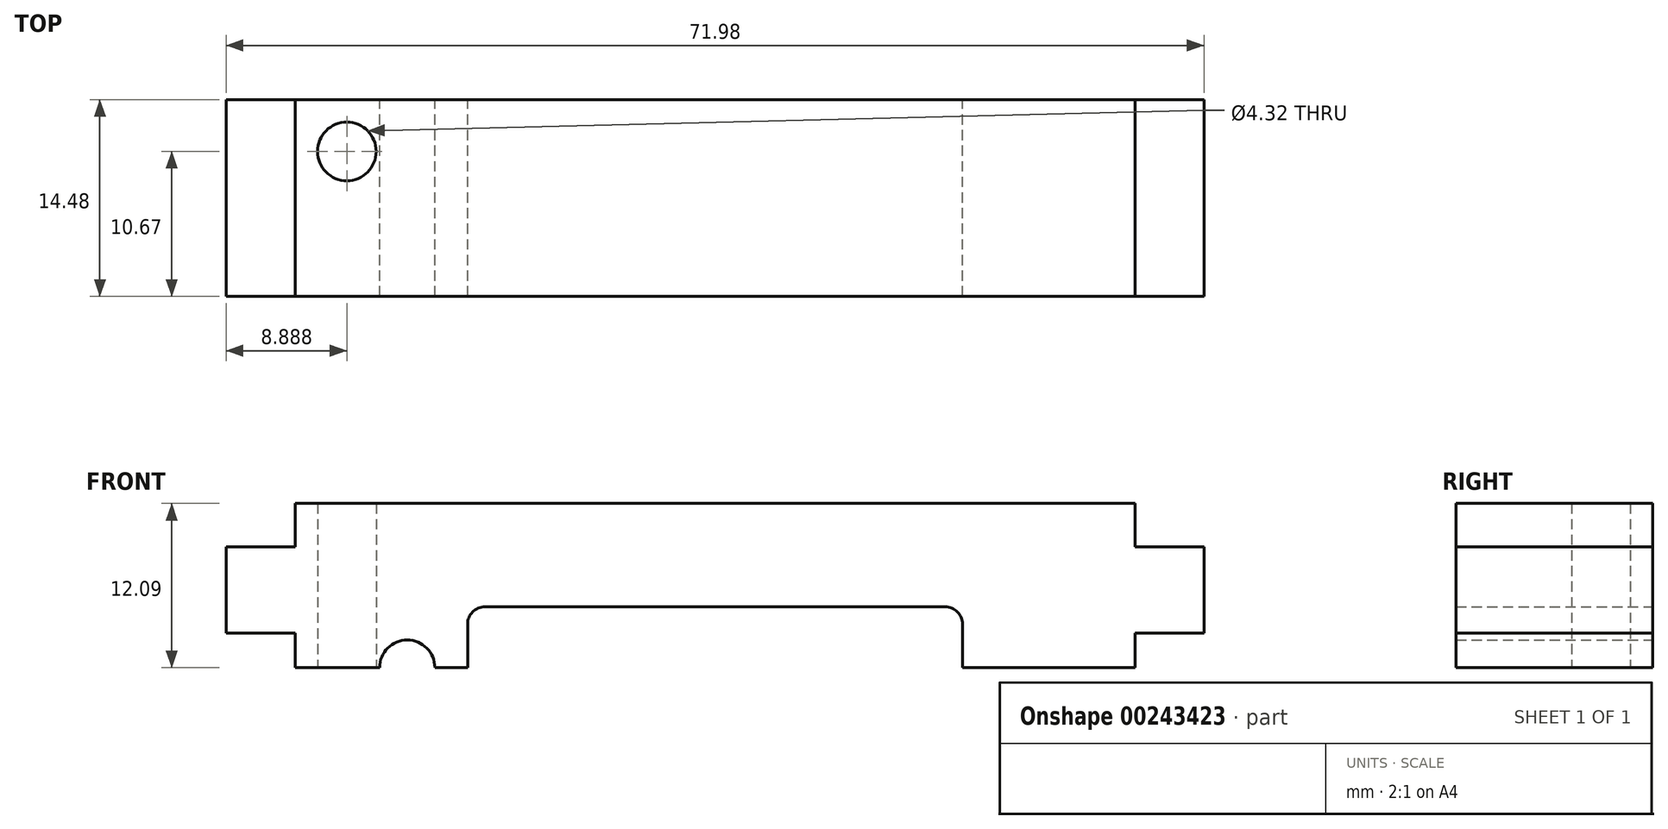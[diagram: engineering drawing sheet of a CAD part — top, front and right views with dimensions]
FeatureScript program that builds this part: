
annotation { "Feature Type Name" : "Feature", "Feature Type Description" : "" }
export const myFeature = defineFeature(function(context is Context, id is Id, definition is map)
    precondition{}
    {
        {
            var Q0;
            Q0=qCreatedBy(makeId("Front.planeOp"),FACE);
            var sketch = newSketch(context, id + "F0", { "sketchPlane" : qUnion([Q0])});
            skLineSegment(sketch, "E0", {"start": v(0, 4.47) * mm, "end": v(-18.21, 4.47) * mm});
            skLineSegment(sketch, "E1", {"start": v(-18.21, 4.47) * mm, "end": v(-18.21, 0) * mm});
            skLineSegment(sketch, "E2", {"start": v(-18.21, 0) * mm, "end": v(-30.91, 0) * mm});
            skLineSegment(sketch, "E3", {"start": v(-30.91, 0) * mm, "end": v(-30.91, 2.54) * mm});
            skLineSegment(sketch, "E4", {"start": v(-30.91, 2.54) * mm, "end": v(-36, 2.54) * mm});
            skLineSegment(sketch, "E5", {"start": v(-36, 2.54) * mm, "end": v(-36, 8.9) * mm});
            skLineSegment(sketch, "E6", {"start": v(-36, 8.9) * mm, "end": v(-30.91, 8.9) * mm});
            skLineSegment(sketch, "E7", {"start": v(-30.91, 8.9) * mm, "end": v(-30.91, 12.1) * mm});
            skLineSegment(sketch, "E8", {"start": v(-30.91, 12.1) * mm, "end": v(0, 12.1) * mm});
            skLineSegment(sketch, "E9.MirrorCS", {"start": v(18.21, 4.47) * mm, "end": v(18.21, 0) * mm});
            skLineSegment(sketch, "E10.MirrorCS", {"start": v(30.91, 8.9) * mm, "end": v(30.91, 12.1) * mm});
            skLineSegment(sketch, "E11.MirrorCS", {"start": v(30.91, 0) * mm, "end": v(30.91, 2.54) * mm});
            skLineSegment(sketch, "E12.MirrorCS", {"start": v(18.21, 0) * mm, "end": v(30.91, 0) * mm});
            skLineSegment(sketch, "E13.MirrorCS", {"start": v(0, 4.47) * mm, "end": v(18.21, 4.47) * mm});
            skLineSegment(sketch, "E14.MirrorCS", {"start": v(36, 8.9) * mm, "end": v(30.91, 8.9) * mm});
            skLineSegment(sketch, "E15.MirrorCS", {"start": v(30.91, 12.1) * mm, "end": v(0, 12.1) * mm});
            skLineSegment(sketch, "E16.MirrorCS", {"start": v(36, 2.54) * mm, "end": v(36, 8.9) * mm});
            skLineSegment(sketch, "E17.MirrorCS", {"start": v(30.91, 2.54) * mm, "end": v(36, 2.54) * mm});
            skSolve(sketch);
        }
        {
            var Q0;
            Q0=makeQuery(id+"F0.imprint","IMPRINT",FACE,{"disambiguationData":[TD([[makeQuery(id+"F0.imprint","IMPRINT",EDGE,{"derivedFrom":sQuery(id+"F0.wireOp",EDGE,"E0")}),-1.0]])]});
            extrude(context, id + "F1", {"entities" : qUnion([Q0]), "depth" : 14.48 * mm});
        }
        {
            var Q0;
            Q0=makeQuery(id+"F1.opExtrude","SWEPT_EDGE",EDGE,{"disambiguationData":[OSD([sQuery(id+"F0.wireOp",EDGE,"E0"),sQuery(id+"F0.wireOp",EDGE,"E1")])]});
            var Q1;
            Q1=makeQuery(id+"F1.opExtrude","SWEPT_EDGE",EDGE,{"disambiguationData":[OSD([sQuery(id+"F0.wireOp",EDGE,"E9.MirrorCS"),sQuery(id+"F0.wireOp",EDGE,"E13.MirrorCS")])]});
            fillet(context, id + "F2", {"entities" : qUnion([Q0, Q1]), "radius" : 1.27 * mm, "tangentPropagation" : true, "allowEdgeOverflow" : false});
        }
        {
            var Q0;
            Q0=makeQuery(id+"F1.opExtrude","SWEPT_FACE",FACE,{"disambiguationData":[OSD([sQuery(id+"F0.wireOp",EDGE,"E2")])]});
            var sketch = newSketch(context, id + "F3", { "sketchPlane" : qUnion([Q0])});
            skCircle(sketch, "E18", {"center": v(-27.1, 3.8) * mm, "radius": 2.16 * mm});
            skCircle(sketch, "E19.MirrorC", {"center": v(27.1, 3.8) * mm, "radius": 2.16 * mm});
            skSolve(sketch);
        }
        {
            var Q0;
            Q0=makeQuery(id+"F3.imprint","IMPRINT",FACE,{"disambiguationData":[TD([[makeQuery(id+"F3.imprint","IMPRINT",EDGE,{"derivedFrom":sQuery(id+"F3.wireOp",EDGE,"E18")}),1.0]])]});
            var Q1;
            Q1=makeQuery(id+"F3.imprint","IMPRINT",FACE,{"disambiguationData":[TD([[makeQuery(id+"F3.imprint","IMPRINT",EDGE,{"derivedFrom":sQuery(id+"F3.wireOp",EDGE,"E19.MirrorC")}),-1.0]])]});
            extrude(context, id + "F4", {"entities" : qUnion([Q0, Q1]), "operationType" : NewBodyOperationType.REMOVE, "endBound" : BoundingType.THROUGH_ALL, "oppositeDirection" : true, "depth" : 25.4 * mm});
        }
        {
            var Q0;
            Q0=makeQuery(id+"F1.opExtrude","CAP_FACE",FACE,{"disambiguationData":[OSD([sQuery(id+"F0.wireOp",EDGE,"E0"),sQuery(id+"F0.wireOp",EDGE,"E1"),sQuery(id+"F0.wireOp",EDGE,"E2"),sQuery(id+"F0.wireOp",EDGE,"E3"),sQuery(id+"F0.wireOp",EDGE,"E4"),sQuery(id+"F0.wireOp",EDGE,"E5"),sQuery(id+"F0.wireOp",EDGE,"E6"),sQuery(id+"F0.wireOp",EDGE,"E7"),sQuery(id+"F0.wireOp",EDGE,"E8"),sQuery(id+"F0.wireOp",EDGE,"E9.MirrorCS"),sQuery(id+"F0.wireOp",EDGE,"E10.MirrorCS"),sQuery(id+"F0.wireOp",EDGE,"E11.MirrorCS"),sQuery(id+"F0.wireOp",EDGE,"E12.MirrorCS"),sQuery(id+"F0.wireOp",EDGE,"E13.MirrorCS"),sQuery(id+"F0.wireOp",EDGE,"E14.MirrorCS"),sQuery(id+"F0.wireOp",EDGE,"E15.MirrorCS"),sQuery(id+"F0.wireOp",EDGE,"E16.MirrorCS"),sQuery(id+"F0.wireOp",EDGE,"E17.MirrorCS")])],"isStart":true});
            var sketch = newSketch(context, id + "F5", { "sketchPlane" : qUnion([Q0])});
            skCircle(sketch, "E20", {"center": v(22.66, 0) * mm, "radius": 2.03 * mm});
            skCircle(sketch, "E21.MirrorC", {"center": v(-22.66, 0) * mm, "radius": 2.03 * mm});
            skSolve(sketch);
        }
        {
            var Q0;
            {var subQ0=sQuery(id+"F5.wireOp",EDGE,"E20");var subQ1=makeQuery(id+"F1.opExtrude","CAP_EDGE",EDGE,{"disambiguationData":[OSD([sQuery(id+"F0.wireOp",EDGE,"E2")])],"isStart":true});var subQ2=makeQuery(id+"F5.imprint","INTERSECT",VERTEX,{"disambiguationData":[OD(0.0)],"derivedFrom":[subQ1,subQ0]});Q0=makeQuery(id+"F5.imprint","IMPRINT",FACE,{"disambiguationData":[TD([[makeQuery(id+"F5.imprint","IMPRINT",EDGE,{"disambiguationData":[TD([[subQ2,1.0]])],"derivedFrom":subQ0}),1.0]])]});}
            var Q1;
            {var subQ0=sQuery(id+"F5.wireOp",EDGE,"E21.MirrorC");var subQ1=makeQuery(id+"F1.opExtrude","CAP_EDGE",EDGE,{"disambiguationData":[OSD([sQuery(id+"F0.wireOp",EDGE,"E12.MirrorCS")])],"isStart":true});var subQ2=makeQuery(id+"F5.imprint","INTERSECT",VERTEX,{"disambiguationData":[OD(0.0)],"derivedFrom":[subQ1,subQ0]});Q1=makeQuery(id+"F5.imprint","IMPRINT",FACE,{"disambiguationData":[TD([[makeQuery(id+"F5.imprint","IMPRINT",EDGE,{"disambiguationData":[TD([[subQ2,1.0]])],"derivedFrom":subQ0}),-1.0]])]});}
            extrude(context, id + "F6", {"entities" : qUnion([Q0, Q1]), "operationType" : NewBodyOperationType.REMOVE, "endBound" : BoundingType.THROUGH_ALL, "oppositeDirection" : true, "depth" : 25.4 * mm});
        }
    });
